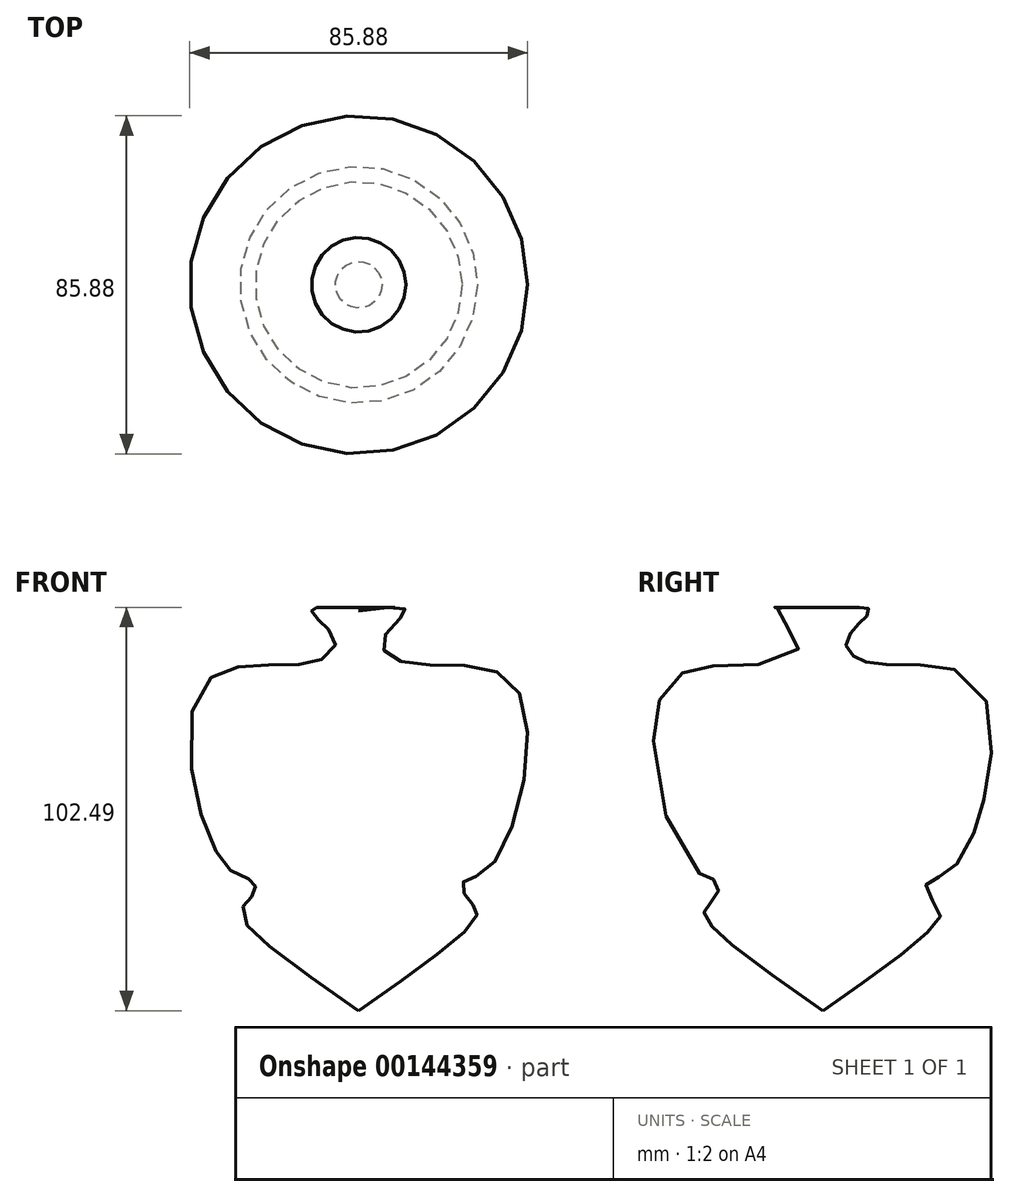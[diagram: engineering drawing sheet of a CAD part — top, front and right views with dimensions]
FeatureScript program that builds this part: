
annotation { "Feature Type Name" : "Feature", "Feature Type Description" : "" }
export const myFeature = defineFeature(function(context is Context, id is Id, definition is map)
    precondition{}
    {
        {
            var Q0;
            Q0=qCreatedBy(makeId("Front.planeOp"),FACE);
            var sketch = newSketch(context, id + "F0", { "sketchPlane" : qUnion([Q0])});
            skLineSegment(sketch, "E0", {"start": v(0, 50) * mm, "end": v(0, -51.6) * mm});
            skFitSpline(sketch, "E1", {"points": [v(0, 50) * mm, v(11.99, 50) * mm, v(6.07, 42.65) * mm, v(12.36, 36.74) * mm, v(39.73, 30.82) * mm, v(33.44, -15.05) * mm, v(26.42, -19.12) * mm, v(27.9, -23.56) * mm, v(30.11, -26.9) * mm, v(0, -51.6) * mm], "startDerivative": vector(182.19, 23.13) * mm, "endDerivative": vector(-247.85, -171.83) * mm});
            skSolve(sketch);
        }
        {
            var Q0;
            Q0=makeQuery(id+"F0.imprint","IMPRINT",FACE,{"disambiguationData":[TD([[makeQuery(id+"F0.imprint","IMPRINT",EDGE,{"derivedFrom":sQuery(id+"F0.wireOp",EDGE,"E0")}),1.0]])]});
            var Q1;
            Q1=sQuery(id+"F0.wireOp",EDGE,"E0");
            revolve(context, id + "F1", {"entities" : qUnion([Q0]), "axis" : qUnion([Q1]), "revolveType" : RevolveType.FULL});
        }
    });
